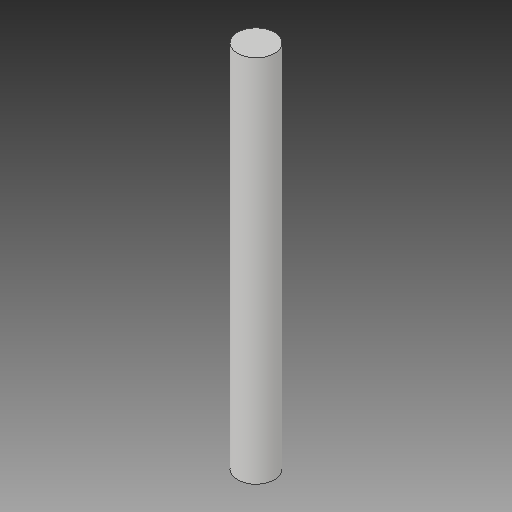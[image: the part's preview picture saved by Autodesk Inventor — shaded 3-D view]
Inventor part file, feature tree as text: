
AUTODESK INVENTOR PART (.ipt)
format: ipt  version: 2019 (Build 230136000, 136)  size: 87,552 bytes
history: native  units: mm
features: other x1, extrude x1, sketch x1
ambient origin geometry x8: Origin, YZ Plane, XZ Plane, XY Plane, X Axis, Y Axis, Z Axis, Center Point
bodies: Body1 (feature_tree)
feature tree (3):
  other  "實體1"
  extrude  "擠出1"  Depth=3.0mm
  sketch  "草圖1"
